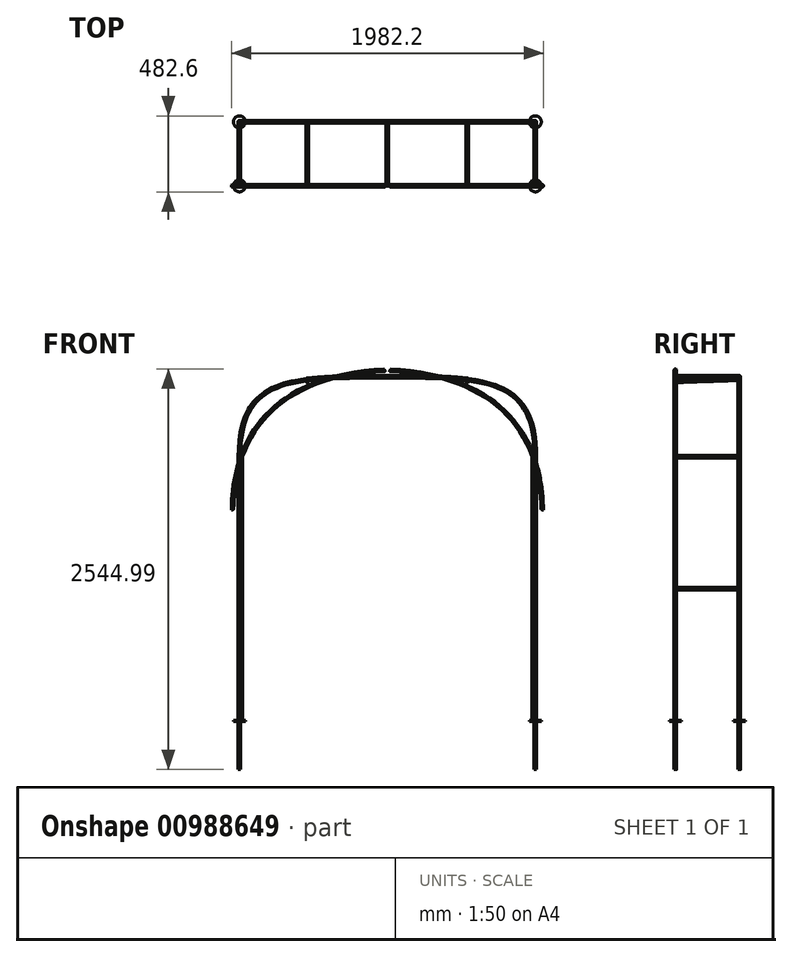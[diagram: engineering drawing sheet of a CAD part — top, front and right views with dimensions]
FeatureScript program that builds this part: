
annotation { "Feature Type Name" : "Feature", "Feature Type Description" : "" }
export const myFeature = defineFeature(function(context is Context, id is Id, definition is map)
    precondition{}
    {
        {
            var Q0;
            Q0=qCreatedBy(makeId("Right.planeOp"),FACE);
            cPlane(context, id + "F0", {"entities" : qUnion([Q0]), "cplaneType" : CPlaneType.OFFSET, "offset" : 939.8 * mm, "oppositeDirection" : true, "width" : 152.4 * mm, "height" : 152.4 * mm});
        }
        {
            var Q0;
            Q0=qCreatedBy(id+"F0.planeOp",FACE);
            var sketch = newSketch(context, id + "F1", { "sketchPlane" : qUnion([Q0])});
            skLineSegment(sketch, "E0", {"start": v(0, 0) * mm, "end": v(-203.2, 0) * mm, "construction": true});
            skLineSegment(sketch, "E1", {"start": v(0, 0) * mm, "end": v(203.2, 0) * mm, "construction": true});
            skLineSegment(sketch, "E2", {"start": v(203.2, 0) * mm, "end": v(203.2, 2184.4) * mm, "construction": true});
            skLineSegment(sketch, "E3", {"start": v(203.2, 2184.4) * mm, "end": v(-203.2, 2184.4) * mm, "construction": true});
            skLineSegment(sketch, "E4", {"start": v(-203.2, 2184.4) * mm, "end": v(-203.2, 0) * mm, "construction": true});
            skSolve(sketch);
        }
        {
            var Q0;
            Q0=qCreatedBy(makeId("Right.planeOp"),FACE);
            var sketch = newSketch(context, id + "F2", { "sketchPlane" : qUnion([Q0])});
            skPoint(sketch, "E5.0", {"position": v(0, 2184.4) * mm});
            skLineSegment(sketch, "E6.0", {"start": v(-203.2, 2184.4) * mm, "end": v(-203.2, 0) * mm, "construction": true});
            skLineSegment(sketch, "E7.0", {"start": v(203.2, 0) * mm, "end": v(203.2, 2184.4) * mm, "construction": true});
            skSolve(sketch);
        }
        {
            var Q0;
            Q0=qCreatedBy(id+"F0.planeOp",FACE);
            var sketch = newSketch(context, id + "F3", { "sketchPlane" : qUnion([Q0])});
            skLineSegment(sketch, "E8", {"start": v(-203.2, 0) * mm, "end": v(-203.2, 1676.4) * mm});
            skLineSegment(sketch, "E9", {"start": v(203.19, 0) * mm, "end": v(203.19, 1676.4) * mm});
            skSolve(sketch);
        }
        {
            var Q0;
            Q0=sQuery(id+"F1.wireOp",EDGE,"E4");
            cPlane(context, id + "F4", {"entities" : qUnion([Q0]), "cplaneType" : CPlaneType.LINE_ANGLE, "offset" : 25.4 * mm, "angle" : 90 * degree, "width" : 152.4 * mm, "height" : 152.4 * mm});
        }
        {
            var Q0;
            Q0=sQuery(id+"F1.wireOp",EDGE,"E2");
            cPlane(context, id + "F5", {"entities" : qUnion([Q0]), "cplaneType" : CPlaneType.LINE_ANGLE, "offset" : 25.4 * mm, "angle" : 90 * degree, "width" : 152.4 * mm, "height" : 152.4 * mm});
        }
        {
            var Q0;
            Q0=qCreatedBy(id+"F4.planeOp",FACE);
            var sketch = newSketch(context, id + "F6", { "sketchPlane" : qUnion([Q0])});
            skFitSpline(sketch, "E10", {"points": [v(940.37, 1354.74) * mm, v(0, 2184.4) * mm], "startDerivative": vector(-41.02, 1524) * mm, "endDerivative": vector(-1828.8, 70.85) * mm});
            skLineSegment(sketch, "E11", {"start": v(609.6, 2160.78) * mm, "end": v(0, 2184.4) * mm, "construction": true});
            skLineSegment(sketch, "E12", {"start": v(940.37, 1354.74) * mm, "end": v(926.7, 1862.74) * mm, "construction": true});
            skSolve(sketch);
        }
        {
            var Q0;
            Q0=qCreatedBy(id+"F5.planeOp",FACE);
            var sketch = newSketch(context, id + "F7", { "sketchPlane" : qUnion([Q0])});
            skFitSpline(sketch, "E13", {"points": [v(939.8, 1676.4) * mm, v(0, 2184.4) * mm], "startDerivative": vector(4.32, 1524) * mm, "endDerivative": vector(-1828.8, 1.65) * mm});
            skLineSegment(sketch, "E14", {"start": v(939.8, 1676.4) * mm, "end": v(941.24, 2184.4) * mm, "construction": true});
            skLineSegment(sketch, "E15", {"start": v(0, 2184.4) * mm, "end": v(609.6, 2183.85) * mm, "construction": true});
            skSolve(sketch);
        }
        {
            var Q0;
            Q0=qCreatedBy(makeId("Top.planeOp"),FACE);
            var sketch = newSketch(context, id + "F8", { "sketchPlane" : qUnion([Q0])});
            skCircle(sketch, "E16", {"center": v(-926.7, -203.2) * mm, "radius": 8 * mm});
            skCircle(sketch, "E17", {"center": v(-939.8, 203.2) * mm, "radius": 8 * mm});
            skSolve(sketch);
        }
        {
            var Q0;
            Q0=makeQuery(id+"F8.imprint","IMPRINT",FACE,{"disambiguationData":[TD([[makeQuery(id+"F8.imprint","IMPRINT",EDGE,{"derivedFrom":sQuery(id+"F8.wireOp",EDGE,"E17")}),1.0]])]});
            var Q1;
            Q1=sQuery(id+"F3.wireOp",EDGE,"E9");
            sweep(context, id + "F9", {"profiles" : qUnion([Q0]), "path" : qUnion([Q1])});
        }
        {
            var Q0;
            Q0=makeQuery(id+"F8.imprint","IMPRINT",FACE,{"disambiguationData":[TD([[makeQuery(id+"F8.imprint","IMPRINT",EDGE,{"derivedFrom":sQuery(id+"F8.wireOp",EDGE,"E16")}),1.0]])]});
            var Q1;
            Q1=sQuery(id+"F3.wireOp",EDGE,"E8");
            sweep(context, id + "F10", {"profiles" : qUnion([Q0]), "path" : qUnion([Q1])});
        }
        {
            var Q0;
            Q0=makeQuery(id+"F10.opSweep","CAP_FACE",FACE,{"disambiguationData":[OSD([sQuery(id+"F3.wireOp",VERTEX,"E8.end"),sQuery(id+"F8.wireOp",EDGE,"E16")])],"isStart":false});
            var Q1;
            Q1=sQuery(id+"F6.wireOp",EDGE,"E10");
            sweep(context, id + "F11", {"operationType" : NewBodyOperationType.ADD, "profiles" : qUnion([Q0]), "path" : qUnion([Q1])});
        }
        {
            var Q0;
            Q0=qCreatedBy(id+"F0.planeOp",FACE);
            var sketch = newSketch(context, id + "F12", { "sketchPlane" : qUnion([Q0])});
            skLineSegment(sketch, "E18", {"start": v(203.19, 838.2) * mm, "end": v(-203.2, 838.2) * mm});
            skSolve(sketch);
        }
        {
            var Q0;
            Q0=qCreatedBy(id+"F0.planeOp",FACE);
            var sketch = newSketch(context, id + "F13", { "sketchPlane" : qUnion([Q0])});
            skLineSegment(sketch, "E19", {"start": v(-203.2, 1676.4) * mm, "end": v(203.19, 1676.4) * mm});
            skSolve(sketch);
        }
        {
            var Q0;
            Q0=makeQuery(id+"F9.opSweep","CAP_FACE",FACE,{"disambiguationData":[OSD([sQuery(id+"F3.wireOp",VERTEX,"E9.end"),sQuery(id+"F8.wireOp",EDGE,"E17")])],"isStart":false});
            var Q1;
            Q1=sQuery(id+"F7.wireOp",EDGE,"E13");
            sweep(context, id + "F14", {"operationType" : NewBodyOperationType.ADD, "profiles" : qUnion([Q0]), "path" : qUnion([Q1])});
        }
        {
            var Q0;
            Q0=qCreatedBy(makeId("Right.planeOp"),FACE);
            var sketch = newSketch(context, id + "F15", { "sketchPlane" : qUnion([Q0])});
            skLineSegment(sketch, "E20", {"start": v(-203.2, 2184.4) * mm, "end": v(203.2, 2184.4) * mm});
            skSolve(sketch);
        }
        {
            var Q0;
            Q0=qCreatedBy(id+"F4.planeOp",FACE);
            var sketch = newSketch(context, id + "F16", { "sketchPlane" : qUnion([Q0])});
            skCircle(sketch, "E21", {"center": v(939.61, 838.34) * mm, "radius": 8 * mm});
            skCircle(sketch, "E22", {"center": v(939.8, 1676.4) * mm, "radius": 8 * mm});
            skSolve(sketch);
        }
        {
            var Q0;
            Q0=makeQuery(id+"F16.imprint","IMPRINT",FACE,{"disambiguationData":[TD([[makeQuery(id+"F16.imprint","IMPRINT",EDGE,{"derivedFrom":sQuery(id+"F16.wireOp",EDGE,"E21")}),1.0]])]});
            var Q1;
            Q1=sQuery(id+"F12.wireOp",EDGE,"E18");
            sweep(context, id + "F17", {"operationType" : NewBodyOperationType.ADD, "profiles" : qUnion([Q0]), "path" : qUnion([Q1])});
        }
        {
            var Q0;
            Q0 = qSketchRegion(id + "F16", true);
            var Q1;
            Q1=sQuery(id+"F13.wireOp",EDGE,"E19");
            sweep(context, id + "F18", {"operationType" : NewBodyOperationType.ADD, "profiles" : qUnion([Q0]), "path" : qUnion([Q1])});
        }
        {
            var Q0;
            Q0=qCreatedBy(id+"F4.planeOp",FACE);
            var sketch = newSketch(context, id + "F19", { "sketchPlane" : qUnion([Q0])});
            skCircle(sketch, "E23", {"center": v(0, 2184.4) * mm, "radius": 8 * mm});
            skSolve(sketch);
        }
        {
            var Q0;
            Q0=makeQuery(id+"F19.imprint","IMPRINT",FACE,{"disambiguationData":[TD([[makeQuery(id+"F19.imprint","IMPRINT",EDGE,{"derivedFrom":sQuery(id+"F19.wireOp",EDGE,"E23")}),1.0]])]});
            var Q1;
            Q1=sQuery(id+"F15.wireOp",EDGE,"E20");
            sweep(context, id + "F20", {"operationType" : NewBodyOperationType.ADD, "profiles" : qUnion([Q0]), "path" : qUnion([Q1])});
        }
        {
            var Q0;
            Q0=qCreatedBy(makeId("Right.planeOp"),FACE);
            cPlane(context, id + "F21", {"entities" : qUnion([Q0]), "cplaneType" : CPlaneType.OFFSET, "offset" : 508 * mm, "oppositeDirection" : true, "width" : 152.4 * mm, "height" : 152.4 * mm});
        }
        {
            var Q0;
            Q0=qCreatedBy(id+"F21.planeOp",FACE);
            var sketch = newSketch(context, id + "F22", { "sketchPlane" : qUnion([Q0])});
            skLineSegment(sketch, "E24", {"start": v(-203.2, 2154.74) * mm, "end": v(203.2, 2169.14) * mm});
            skSolve(sketch);
        }
        {
            var Q0;
            Q0=qCreatedBy(id+"F4.planeOp",FACE);
            var sketch = newSketch(context, id + "F23", { "sketchPlane" : qUnion([Q0])});
            skCircle(sketch, "E25", {"center": v(508, 2154.74) * mm, "radius": 7.62 * mm});
            skSolve(sketch);
        }
        {
            var Q0;
            Q0 = qSketchRegion(id + "F23", true);
            var Q1;
            Q1=sQuery(id+"F22.wireOp",EDGE,"E24");
            sweep(context, id + "F24", {"operationType" : NewBodyOperationType.ADD, "profiles" : qUnion([Q0]), "path" : qUnion([Q1])});
        }
        {
            var Q0;
            Q0=qCreatedBy(makeId("Top.planeOp"),FACE);
            var sketch = newSketch(context, id + "F25", { "sketchPlane" : qUnion([Q0])});
            skCircle(sketch, "E26", {"center": v(-939.8, -203.2) * mm, "radius": 38.1 * mm});
            skCircle(sketch, "E27", {"center": v(-939.8, 203.2) * mm, "radius": 38.1 * mm});
            skSolve(sketch);
        }
        {
            var Q0;
            Q0 = qSketchRegion(id + "F25", true);
            extrude(context, id + "F26", {"entities" : qUnion([Q0]), "operationType" : NewBodyOperationType.ADD, "oppositeDirection" : true, "depth" : 6.35 * mm, "offsetDistance" : 25.4 * mm});
        }
        {
            var Q0;
            Q0=makeQuery(id+"F26.opExtrude","CAP_FACE",FACE,{"disambiguationData":[OSD([sQuery(id+"F25.wireOp",EDGE,"E26")])],"isStart":false});
            var sketch = newSketch(context, id + "F27", { "sketchPlane" : qUnion([Q0])});
            skCircle(sketch, "E28", {"center": v(-939.8, 203.2) * mm, "radius": 8 * mm});
            skSolve(sketch);
        }
        {
            var Q0;
            Q0=makeQuery(id+"F27.imprint","IMPRINT",FACE,{"disambiguationData":[TD([[makeQuery(id+"F27.imprint","IMPRINT",EDGE,{"derivedFrom":sQuery(id+"F27.wireOp",EDGE,"E28")}),1.0]])]});
            extrude(context, id + "F28", {"entities" : qUnion([Q0]), "operationType" : NewBodyOperationType.ADD, "depth" : 304.8 * mm, "offsetDistance" : 25.4 * mm});
        }
        {
            var Q0;
            Q0=makeQuery(id+"F26.opExtrude","CAP_FACE",FACE,{"disambiguationData":[OSD([sQuery(id+"F25.wireOp",EDGE,"E27")])],"isStart":false});
            var sketch = newSketch(context, id + "F29", { "sketchPlane" : qUnion([Q0])});
            skCircle(sketch, "E29", {"center": v(-939.8, -203.2) * mm, "radius": 8 * mm});
            skSolve(sketch);
        }
        {
            var Q0;
            Q0=makeQuery(id+"F29.imprint","IMPRINT",FACE,{"disambiguationData":[TD([[makeQuery(id+"F29.imprint","IMPRINT",EDGE,{"derivedFrom":sQuery(id+"F29.wireOp",EDGE,"E29")}),1.0]])]});
            extrude(context, id + "F30", {"entities" : qUnion([Q0]), "operationType" : NewBodyOperationType.ADD, "depth" : 304.8 * mm, "offsetDistance" : 25.4 * mm});
        }
        {
            var Q0;
            Q0=makeQuery(id+"F9.opSweep","SWEPT_BODY",BODY,{"disambiguationData":[OSD([sQuery(id+"F3.wireOp",EDGE,"E9"),sQuery(id+"F8.wireOp",EDGE,"E17")])]});
            var Q1;
            Q1=qCreatedBy(makeId("Right.planeOp"),FACE);
            mirror(context, id + "F31", {"operationType" : NewBodyOperationType.ADD, "entities" : qUnion([Q0]), "mirrorPlane" : qUnion([Q1])});
        }
    });
